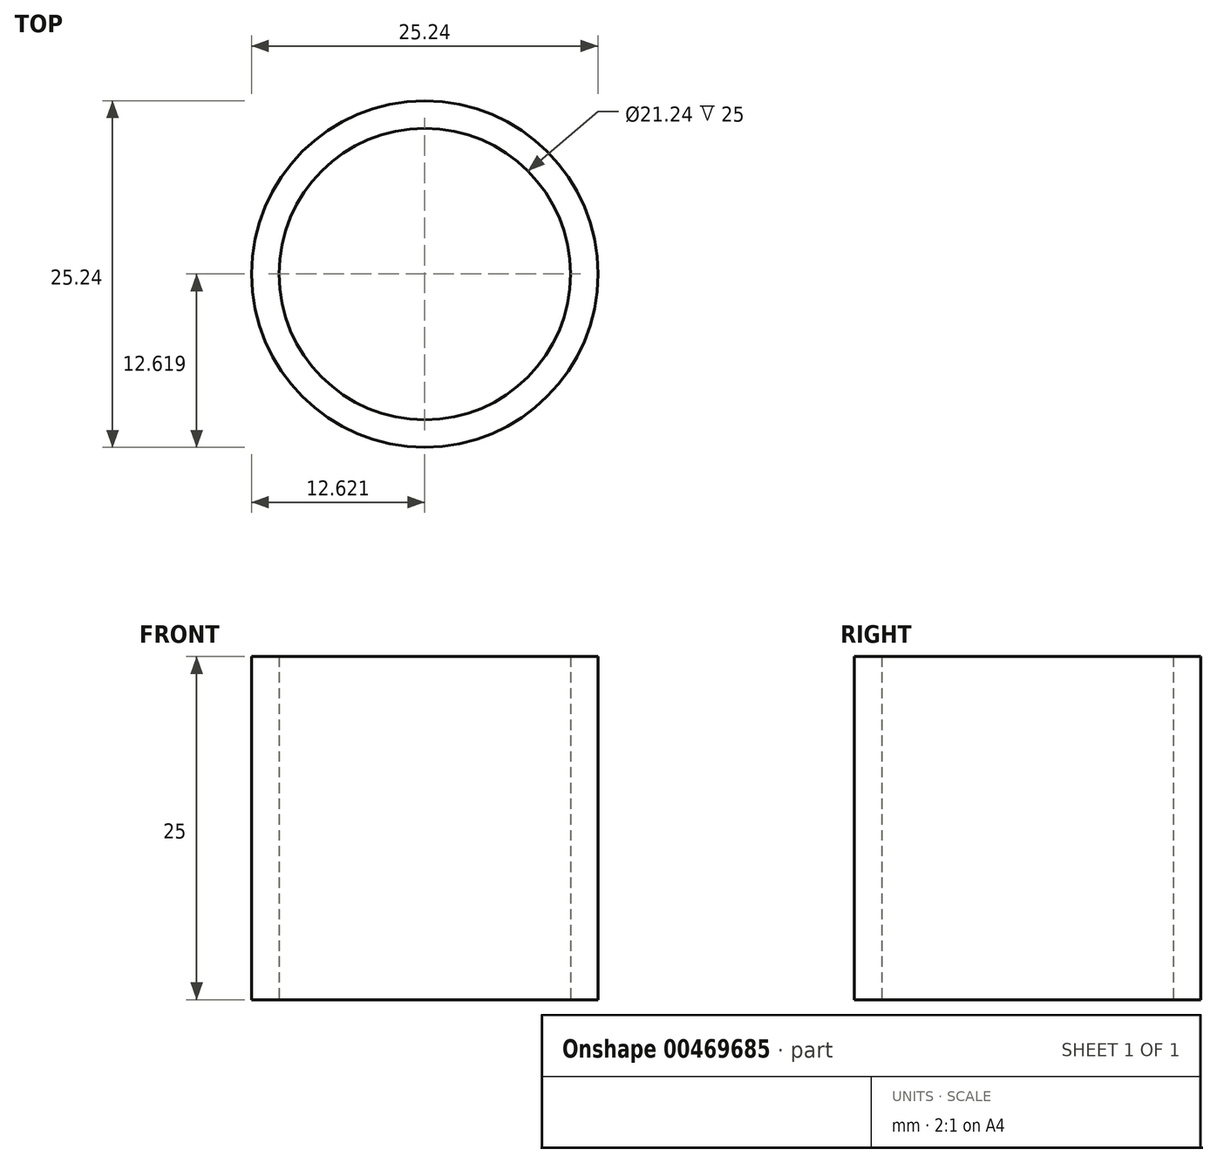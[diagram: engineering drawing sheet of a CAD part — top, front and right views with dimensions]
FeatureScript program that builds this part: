
annotation { "Feature Type Name" : "Feature", "Feature Type Description" : "" }
export const myFeature = defineFeature(function(context is Context, id is Id, definition is map)
    precondition{}
    {
        {
            var Q0;
            Q0=qCreatedBy(makeId("Top.planeOp"),FACE);
            var sketch = newSketch(context, id + "F0", { "sketchPlane" : qUnion([Q0])});
            skCircle(sketch, "E0", {"center": v(0.07, -0.07) * mm, "radius": 12.62 * mm});
            skCircle(sketch, "E1", {"center": v(0.07, -0.07) * mm, "radius": 10.62 * mm});
            skSolve(sketch);
        }
        {
            var Q0;
            Q0=makeQuery(id+"F0.imprint","IMPRINT",FACE,{"disambiguationData":[TD([[makeQuery(id+"F0.imprint","IMPRINT",EDGE,{"derivedFrom":sQuery(id+"F0.wireOp",EDGE,"E0")}),1.0]])]});
            extrude(context, id + "F1", {"entities" : qUnion([Q0]), "depth" : 25 * mm, "offsetDistance" : 25 * mm});
        }
    });
